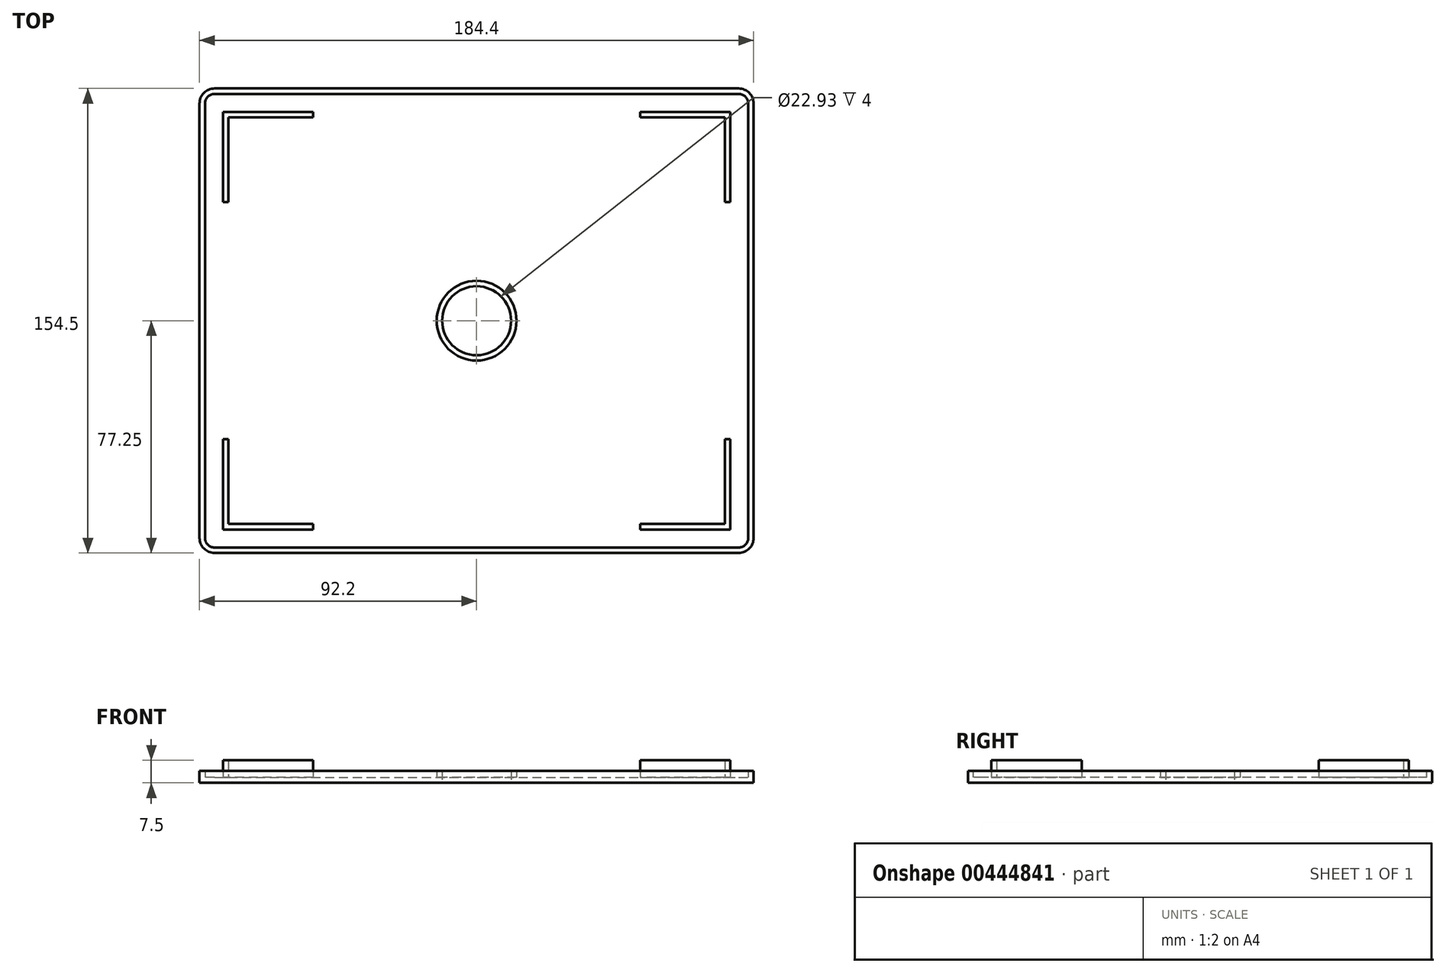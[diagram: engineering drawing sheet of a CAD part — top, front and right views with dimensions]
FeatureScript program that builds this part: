
annotation { "Feature Type Name" : "Feature", "Feature Type Description" : "" }
export const myFeature = defineFeature(function(context is Context, id is Id, definition is map)
    precondition{}
    {
        {
            var Q0;
            Q0=qCreatedBy(makeId("Top.planeOp"),FACE);
            var sketch = newSketch(context, id + "F0", { "sketchPlane" : qUnion([Q0])});
            skLineSegment(sketch, "E0.rect.bottom", {"start": v(-92.2, 77.25) * mm, "end": v(92.2, 77.25) * mm});
            skLineSegment(sketch, "E0.rect.top", {"start": v(-92.2, -77.25) * mm, "end": v(92.2, -77.25) * mm});
            skLineSegment(sketch, "E0.rect.left", {"start": v(-92.2, 77.25) * mm, "end": v(-92.2, -77.25) * mm});
            skLineSegment(sketch, "E0.rect.right", {"start": v(92.2, 77.25) * mm, "end": v(92.2, -77.25) * mm});
            skPoint(sketch, "E0.rect.middle", {"position": v(0, 0) * mm});
            skCircle(sketch, "E1", {"center": v(0, 0) * mm, "radius": 11.47 * mm});
            skSolve(sketch);
        }
        {
            var Q0;
            Q0=qSketchRegion(id+"F0",true);
            extrude(context, id + "F1", {"entities" : qUnion([Q0]), "depth" : 4 * mm});
        }
        {
            var Q0;
            Q0=makeQuery(id+"F1.opExtrude","SWEPT_EDGE",EDGE,{"disambiguationData":[OSD([sQuery(id+"F0.wireOp",EDGE,"E0.rect.top"),sQuery(id+"F0.wireOp",EDGE,"E0.rect.left")])]});
            var Q1;
            Q1=makeQuery(id+"F1.opExtrude","SWEPT_EDGE",EDGE,{"disambiguationData":[OSD([sQuery(id+"F0.wireOp",EDGE,"E0.rect.bottom"),sQuery(id+"F0.wireOp",EDGE,"E0.rect.left")])]});
            var Q2;
            Q2=makeQuery(id+"F1.opExtrude","SWEPT_EDGE",EDGE,{"disambiguationData":[OSD([sQuery(id+"F0.wireOp",EDGE,"E0.rect.top"),sQuery(id+"F0.wireOp",EDGE,"E0.rect.right")])]});
            var Q3;
            Q3=makeQuery(id+"F1.opExtrude","SWEPT_EDGE",EDGE,{"disambiguationData":[OSD([sQuery(id+"F0.wireOp",EDGE,"E0.rect.bottom"),sQuery(id+"F0.wireOp",EDGE,"E0.rect.right")])]});
            fillet(context, id + "F2", {"entities" : qUnion([Q0, Q1, Q2, Q3]), "radius" : 5 * mm, "tangentPropagation" : true, "allowEdgeOverflow" : false});
        }
        {
            var Q0;
            Q0=makeQuery(id+"F1.opExtrude","CAP_FACE",FACE,{"disambiguationData":[OSD([sQuery(id+"F0.wireOp",EDGE,"E0.rect.bottom"),sQuery(id+"F0.wireOp",EDGE,"E0.rect.top"),sQuery(id+"F0.wireOp",EDGE,"E0.rect.left"),sQuery(id+"F0.wireOp",EDGE,"E0.rect.right")])],"isStart":false});
            shell(context, id + "F3", {"entities" : qUnion([Q0]), "thickness" : 1.8 * mm});
        }
        {
            var Q0;
            Q0=makeQuery(id+"F3.opShell","OFFSET_FACE",FACE,{"disambiguationData":[OSD([sQuery(id+"F0.wireOp",EDGE,"E0.rect.bottom"),sQuery(id+"F0.wireOp",EDGE,"E0.rect.top"),sQuery(id+"F0.wireOp",EDGE,"E0.rect.left"),sQuery(id+"F0.wireOp",EDGE,"E0.rect.right")])]});
            var sketch = newSketch(context, id + "F4", { "sketchPlane" : qUnion([Q0])});
            skLineSegment(sketch, "E2", {"start": v(-84.4, -69.45) * mm, "end": v(-84.4, -39.45) * mm});
            skLineSegment(sketch, "E3", {"start": v(-84.4, -39.45) * mm, "end": v(-82.6, -39.45) * mm});
            skLineSegment(sketch, "E4", {"start": v(-82.6, -39.45) * mm, "end": v(-82.6, -67.65) * mm});
            skLineSegment(sketch, "E5", {"start": v(-82.6, -67.65) * mm, "end": v(-54.4, -67.65) * mm});
            skLineSegment(sketch, "E6", {"start": v(-54.4, -67.65) * mm, "end": v(-54.4, -69.45) * mm});
            skLineSegment(sketch, "E7", {"start": v(-54.4, -69.45) * mm, "end": v(-84.4, -69.45) * mm});
            skLineSegment(sketch, "E8.MirrorCS", {"start": v(-54.4, 67.65) * mm, "end": v(-54.4, 69.45) * mm});
            skLineSegment(sketch, "E9.MirrorCS", {"start": v(-54.4, 69.45) * mm, "end": v(-84.4, 69.45) * mm});
            skLineSegment(sketch, "E10.MirrorCS", {"start": v(-82.6, 67.65) * mm, "end": v(-54.4, 67.65) * mm});
            skLineSegment(sketch, "E11.MirrorCS", {"start": v(-82.6, 39.45) * mm, "end": v(-82.6, 67.65) * mm});
            skLineSegment(sketch, "E12.MirrorCS", {"start": v(-84.4, 69.45) * mm, "end": v(-84.4, 39.45) * mm});
            skLineSegment(sketch, "E13.MirrorCS", {"start": v(-84.4, 39.45) * mm, "end": v(-82.6, 39.45) * mm});
            skLineSegment(sketch, "E14.MirrorCS", {"start": v(84.4, -39.45) * mm, "end": v(82.6, -39.45) * mm});
            skLineSegment(sketch, "E15.MirrorCS", {"start": v(84.4, 39.45) * mm, "end": v(82.6, 39.45) * mm});
            skLineSegment(sketch, "E16.MirrorCS", {"start": v(54.4, -67.65) * mm, "end": v(54.4, -69.45) * mm});
            skLineSegment(sketch, "E17.MirrorCS", {"start": v(54.4, 67.65) * mm, "end": v(54.4, 69.45) * mm});
            skLineSegment(sketch, "E18.MirrorCS", {"start": v(84.4, 69.45) * mm, "end": v(84.4, 39.45) * mm});
            skLineSegment(sketch, "E19.MirrorCS", {"start": v(54.4, 69.45) * mm, "end": v(84.4, 69.45) * mm});
            skLineSegment(sketch, "E20.MirrorCS", {"start": v(84.4, -69.45) * mm, "end": v(84.4, -39.45) * mm});
            skLineSegment(sketch, "E21.MirrorCS", {"start": v(82.6, 39.45) * mm, "end": v(82.6, 67.65) * mm});
            skLineSegment(sketch, "E22.MirrorCS", {"start": v(82.6, 67.65) * mm, "end": v(54.4, 67.65) * mm});
            skLineSegment(sketch, "E23.MirrorCS", {"start": v(82.6, -67.65) * mm, "end": v(54.4, -67.65) * mm});
            skLineSegment(sketch, "E24.MirrorCS", {"start": v(54.4, -69.45) * mm, "end": v(84.4, -69.45) * mm});
            skLineSegment(sketch, "E25.MirrorCS", {"start": v(82.6, -39.45) * mm, "end": v(82.6, -67.65) * mm});
            skSolve(sketch);
        }
        {
            var Q0;
            Q0=qSketchRegion(id+"F4",true);
            extrude(context, id + "F5", {"entities" : qUnion([Q0]), "operationType" : NewBodyOperationType.ADD, "depth" : 5.7 * mm});
        }
    });
